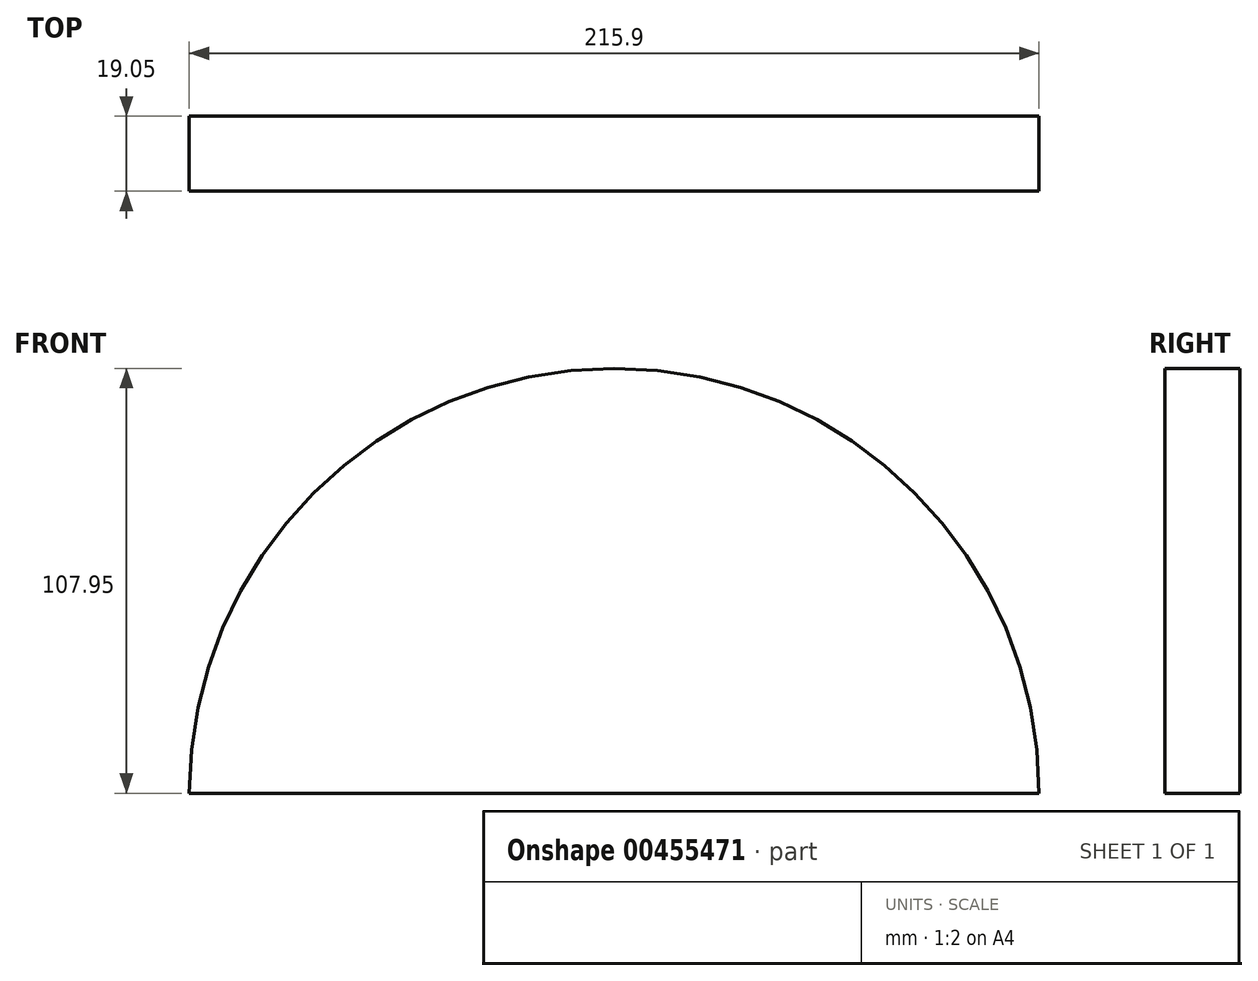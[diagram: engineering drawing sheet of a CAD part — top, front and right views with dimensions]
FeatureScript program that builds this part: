
annotation { "Feature Type Name" : "Feature", "Feature Type Description" : "" }
export const myFeature = defineFeature(function(context is Context, id is Id, definition is map)
    precondition{}
    {
        {
            var Q0;
            Q0=qCreatedBy(makeId("Front.planeOp"),FACE);
            var sketch = newSketch(context, id + "F0", { "sketchPlane" : qUnion([Q0])});
            skArc(sketch, "E0", {"start": v(107.95, 0) * mm, "mid": v(0, 107.95) * mm, "end": v(-107.95, 0) * mm});
            skLineSegment(sketch, "E1", {"start": v(-107.95, 0) * mm, "end": v(107.95, 0) * mm});
            skSolve(sketch);
        }
        {
            var Q0;
            Q0 = qSketchRegion(id + "F0", true);
            extrude(context, id + "F1", {"entities" : qUnion([Q0]), "depth" : 19.05 * mm});
        }
    });
